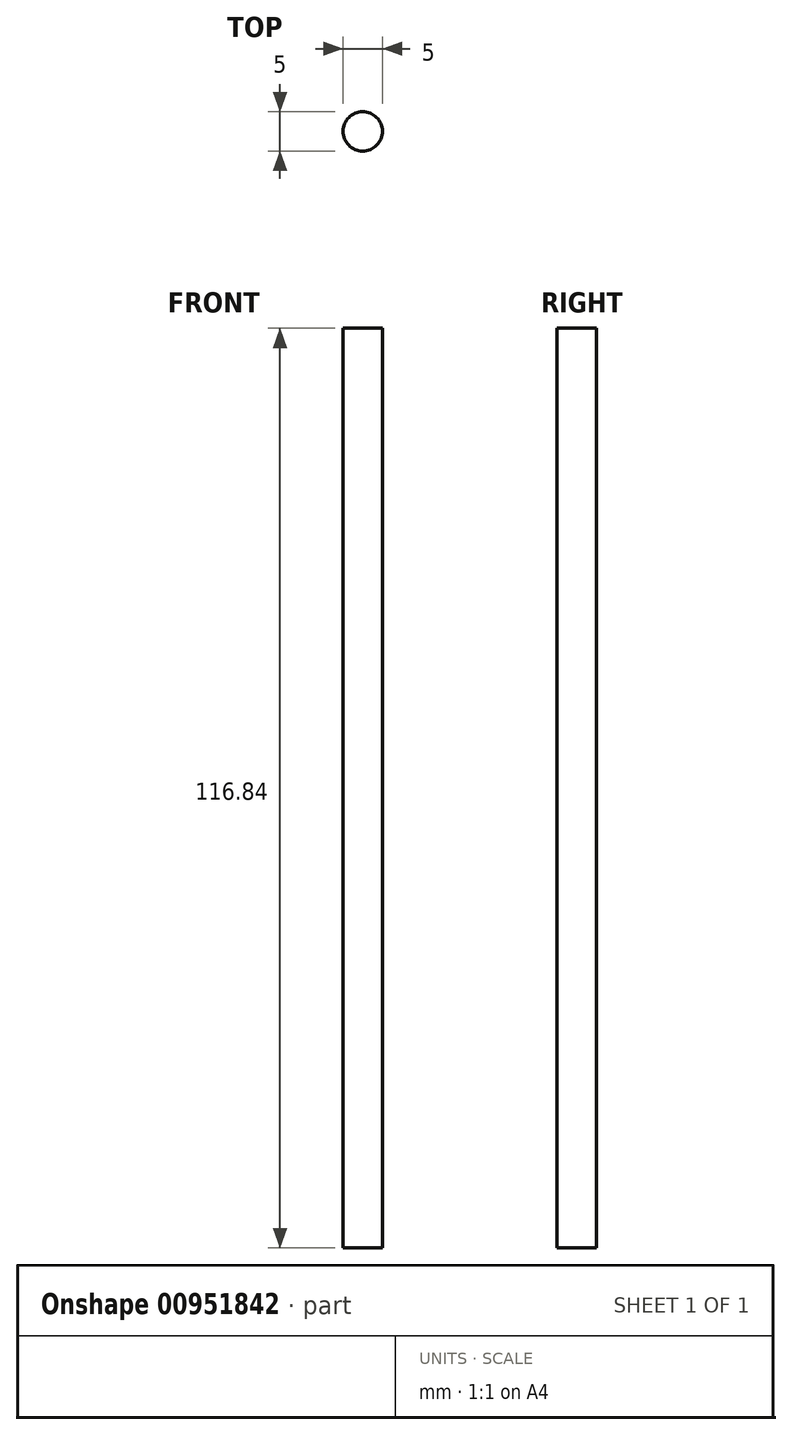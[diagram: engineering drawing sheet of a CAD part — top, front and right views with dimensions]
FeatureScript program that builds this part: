
annotation { "Feature Type Name" : "Feature", "Feature Type Description" : "" }
export const myFeature = defineFeature(function(context is Context, id is Id, definition is map)
    precondition{}
    {
        {
            var Q0;
            Q0=qCreatedBy(makeId("Top.planeOp"),FACE);
            var sketch = newSketch(context, id + "F0", { "sketchPlane" : qUnion([Q0])});
            skCircle(sketch, "E0", {"center": v(0, 0) * mm, "radius": 2.5 * mm});
            skSolve(sketch);
        }
        {
            var Q0;
            Q0=makeQuery(id+"F0.imprint","IMPRINT",FACE,{"disambiguationData":[TD([[makeQuery(id+"F0.imprint","IMPRINT",EDGE,{"derivedFrom":sQuery(id+"F0.wireOp",EDGE,"E0")}),1.0]])]});
            extrude(context, id + "F1", {"entities" : qUnion([Q0]), "endBound" : BoundingType.SYMMETRIC, "depth" : 116.84 * mm, "offsetDistance" : 25.4 * mm});
        }
    });
